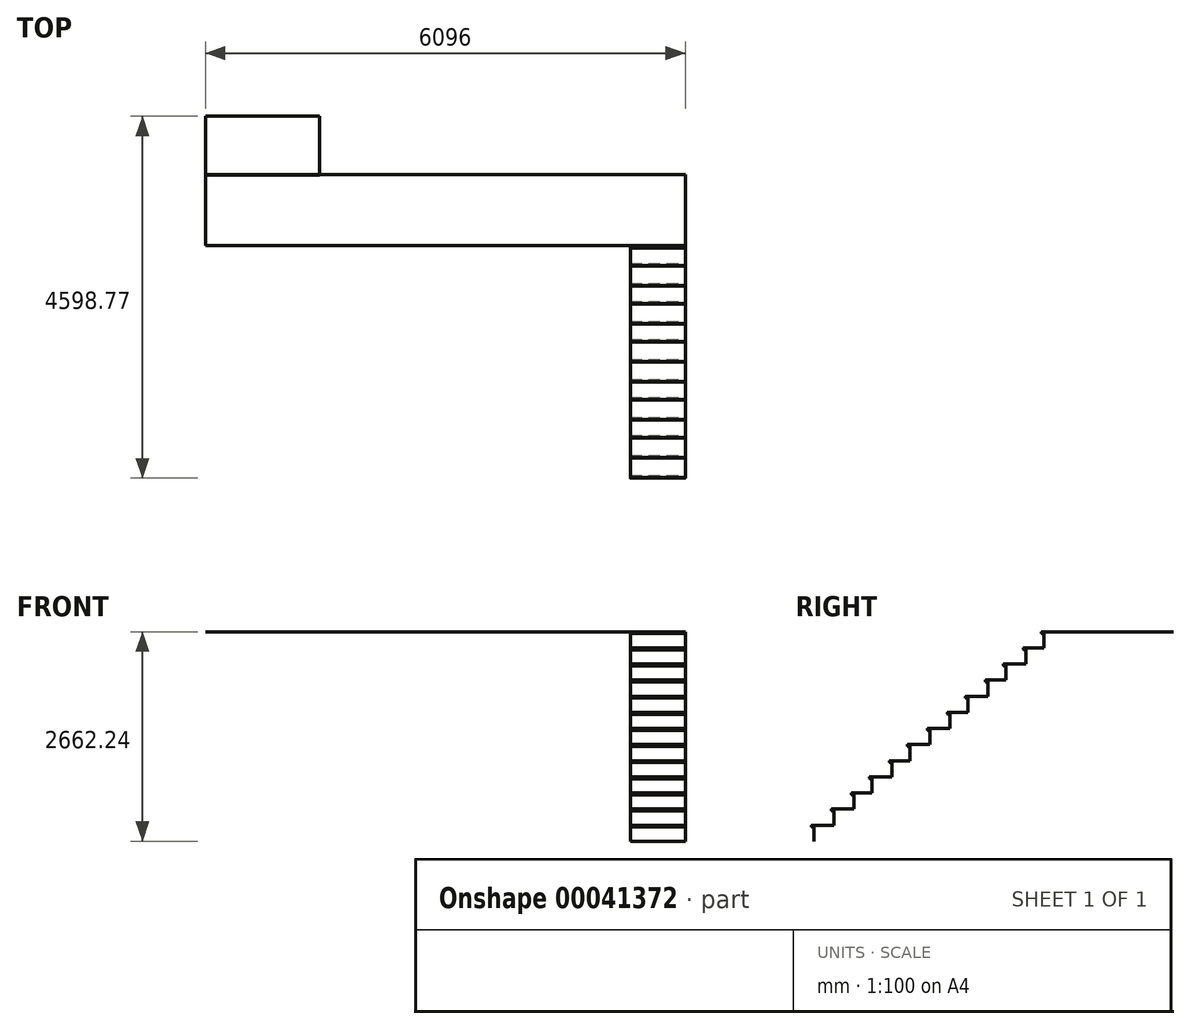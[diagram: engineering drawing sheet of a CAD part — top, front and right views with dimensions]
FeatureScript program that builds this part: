
annotation { "Feature Type Name" : "Feature", "Feature Type Description" : "" }
export const myFeature = defineFeature(function(context is Context, id is Id, definition is map)
    precondition{}
    {
        {
            var Q0;
            Q0=qCreatedBy(makeId("Top.planeOp"),FACE);
            var sketch = newSketch(context, id + "F0", { "sketchPlane" : qUnion([Q0])});
            skLineSegment(sketch, "E0", {"start": v(0, 0) * mm, "end": v(0, 1644.65) * mm});
            skLineSegment(sketch, "E1", {"start": v(0, 1644.65) * mm, "end": v(1447.8, 1644.65) * mm});
            skLineSegment(sketch, "E2", {"start": v(1447.8, 1644.65) * mm, "end": v(1447.8, 895.35) * mm});
            skLineSegment(sketch, "E3", {"start": v(1447.8, 895.35) * mm, "end": v(6096, 895.35) * mm});
            skLineSegment(sketch, "E4", {"start": v(6096, 895.35) * mm, "end": v(6096, 0) * mm});
            skLineSegment(sketch, "E5", {"start": v(0, 0) * mm, "end": v(5397.5, 0) * mm});
            skSolve(sketch);
        }
        {
            var Q0;
            Q0=qCreatedBy(makeId("Right.planeOp"),FACE);
            var Q1;
            Q1=sQuery(id+"F0.wireOp",VERTEX,"E5.end");
            cPlane(context, id + "F1", {"entities" : qUnion([Q0, Q1]), "cplaneType" : CPlaneType.PLANE_POINT, "offset" : 152.4 * mm, "width" : 152.4 * mm, "height" : 152.4 * mm});
        }
        {
            var Q0;
            Q0=qCreatedBy(id+"F1.planeOp",FACE);
            var sketch = newSketch(context, id + "F2", { "sketchPlane" : qUnion([Q0])});
            skLineSegment(sketch, "E6", {"start": v(-25.4, 0) * mm, "end": v(0, 0) * mm});
            skLineSegment(sketch, "E7", {"start": v(-25.4, -23.81) * mm, "end": v(0, -23.81) * mm});
            skLineSegment(sketch, "E8", {"start": v(0, -23.81) * mm, "end": v(0, -204.79) * mm});
            skArc(sketch, "E9", {"start": v(-25.4, 0) * mm, "mid": v(-31.75, -11.9) * mm, "end": v(-25.4, -23.81) * mm});
            skLineSegment(sketch, "E10", {"start": v(-31.75, -11.9) * mm, "end": v(-31.75, 17.78) * mm, "construction": true});
            skLineSegment(sketch, "E11", {"start": v(0, -204.79) * mm, "end": v(-254, -204.79) * mm});
            skArc(sketch, "E12", {"start": v(-254, -204.79) * mm, "mid": v(-260.35, -216.7) * mm, "end": v(-254, -228.6) * mm});
            skLineSegment(sketch, "E13", {"start": v(-254, -228.6) * mm, "end": v(-228.6, -228.6) * mm});
            skLineSegment(sketch, "E14", {"start": v(-228.6, -228.6) * mm, "end": v(-228.6, -409.58) * mm});
            skLineSegment(sketch, "E15", {"start": v(-228.6, -409.58) * mm, "end": v(-482.6, -409.58) * mm});
            skLineSegment(sketch, "E16", {"start": v(-260.35, -216.7) * mm, "end": v(-260.35, -170.19) * mm, "construction": true});
            skLineSegment(sketch, "E17", {"start": v(-482.6, -433.39) * mm, "end": v(-482.6, -614.36) * mm});
            skLineSegment(sketch, "E18", {"start": v(-711.2, -819.15) * mm, "end": v(-965.2, -819.15) * mm});
            skLineSegment(sketch, "E19", {"start": v(-482.6, -614.36) * mm, "end": v(-736.6, -614.36) * mm});
            skLineSegment(sketch, "E20", {"start": v(-711.2, -638.18) * mm, "end": v(-711.2, -819.15) * mm});
            skLineSegment(sketch, "E21", {"start": v(-742.95, -940.84) * mm, "end": v(-742.95, -626.27) * mm, "construction": true});
            skArc(sketch, "E22", {"start": v(-736.6, -614.36) * mm, "mid": v(-742.95, -626.27) * mm, "end": v(-736.6, -638.18) * mm});
            skLineSegment(sketch, "E23", {"start": v(-736.6, -638.18) * mm, "end": v(-711.2, -638.18) * mm});
            skArc(sketch, "E24", {"start": v(-508, -409.58) * mm, "mid": v(-514.35, -421.48) * mm, "end": v(-508, -433.39) * mm});
            skLineSegment(sketch, "E25", {"start": v(-508, -433.39) * mm, "end": v(-482.6, -433.39) * mm});
            skLineSegment(sketch, "E26", {"start": v(-508, -409.58) * mm, "end": v(-482.6, -409.58) * mm});
            skLineSegment(sketch, "E27", {"start": v(-514.35, -752.87) * mm, "end": v(-514.35, -421.48) * mm, "construction": true});
            skLineSegment(sketch, "E28", {"start": v(-1473.2, -1252.54) * mm, "end": v(-1447.8, -1252.54) * mm});
            skLineSegment(sketch, "E29", {"start": v(-1479.55, -1790.24) * mm, "end": v(-1479.55, -1240.63) * mm, "construction": true});
            skLineSegment(sketch, "E30", {"start": v(-965.2, -842.96) * mm, "end": v(-965.2, -1023.94) * mm});
            skLineSegment(sketch, "E31", {"start": v(-965.2, -1023.94) * mm, "end": v(-1219.2, -1023.94) * mm});
            skLineSegment(sketch, "E32", {"start": v(-1447.8, -1433.51) * mm, "end": v(-1701.8, -1433.51) * mm});
            skLineSegment(sketch, "E33", {"start": v(-1447.8, -1252.54) * mm, "end": v(-1447.8, -1433.51) * mm});
            skLineSegment(sketch, "E34", {"start": v(-1193.8, -1228.73) * mm, "end": v(-1447.8, -1228.73) * mm});
            skLineSegment(sketch, "E35", {"start": v(-1193.8, -1047.75) * mm, "end": v(-1193.8, -1228.73) * mm});
            skArc(sketch, "E36", {"start": v(-1473.2, -1228.73) * mm, "mid": v(-1479.55, -1240.63) * mm, "end": v(-1473.2, -1252.54) * mm});
            skLineSegment(sketch, "E37", {"start": v(-1473.2, -1228.73) * mm, "end": v(-1447.8, -1228.73) * mm});
            skArc(sketch, "E38", {"start": v(-1219.2, -1023.94) * mm, "mid": v(-1225.55, -1035.84) * mm, "end": v(-1219.2, -1047.75) * mm});
            skLineSegment(sketch, "E39", {"start": v(-1225.55, -1207.55) * mm, "end": v(-1225.55, -1035.84) * mm, "construction": true});
            skLineSegment(sketch, "E40", {"start": v(-1219.2, -1047.75) * mm, "end": v(-1193.8, -1047.75) * mm});
            skLineSegment(sketch, "E41", {"start": v(-990.6, -842.96) * mm, "end": v(-965.2, -842.96) * mm});
            skArc(sketch, "E42", {"start": v(-990.6, -819.15) * mm, "mid": v(-996.95, -831.06) * mm, "end": v(-990.6, -842.96) * mm});
            skLineSegment(sketch, "E43", {"start": v(-996.95, -1019.59) * mm, "end": v(-996.95, -831.06) * mm, "construction": true});
            skLineSegment(sketch, "E44", {"start": v(-990.6, -819.15) * mm, "end": v(-965.2, -819.15) * mm});
            skLineSegment(sketch, "E45", {"start": v(-2413, -2252.66) * mm, "end": v(-2667, -2252.66) * mm});
            skLineSegment(sketch, "E46", {"start": v(-2667, -2457.45) * mm, "end": v(-2921, -2457.45) * mm});
            skLineSegment(sketch, "E47", {"start": v(-2216.15, -1855) * mm, "end": v(-2216.15, -1794.57) * mm, "construction": true});
            skLineSegment(sketch, "E48", {"start": v(-2184.4, -1866.9) * mm, "end": v(-2184.4, -2047.88) * mm});
            skLineSegment(sketch, "E49", {"start": v(-2698.75, -2565.22) * mm, "end": v(-2698.75, -2264.57) * mm, "construction": true});
            skLineSegment(sketch, "E50", {"start": v(-1701.8, -1638.3) * mm, "end": v(-1955.8, -1638.3) * mm});
            skLineSegment(sketch, "E51", {"start": v(-1930.4, -1662.11) * mm, "end": v(-1930.4, -1843.09) * mm});
            skLineSegment(sketch, "E52", {"start": v(-1962.15, -1715.82) * mm, "end": v(-1962.15, -1650.2) * mm, "construction": true});
            skLineSegment(sketch, "E53", {"start": v(-1733.55, -1527.85) * mm, "end": v(-1733.55, -1445.42) * mm, "construction": true});
            skLineSegment(sketch, "E54", {"start": v(-1930.4, -1843.09) * mm, "end": v(-2184.4, -1843.09) * mm});
            skLineSegment(sketch, "E55", {"start": v(-2184.4, -2047.88) * mm, "end": v(-2438.4, -2047.88) * mm});
            skLineSegment(sketch, "E56", {"start": v(-1701.8, -1457.33) * mm, "end": v(-1701.8, -1638.3) * mm});
            skLineSegment(sketch, "E57", {"start": v(-2667, -2276.48) * mm, "end": v(-2667, -2457.45) * mm});
            skLineSegment(sketch, "E58", {"start": v(-2413, -2071.69) * mm, "end": v(-2413, -2252.66) * mm});
            skLineSegment(sketch, "E59", {"start": v(-2444.75, -2059.78) * mm, "end": v(-2444.75, -1982.54) * mm, "construction": true});
            skArc(sketch, "E60", {"start": v(-2692.4, -2252.66) * mm, "mid": v(-2698.75, -2264.57) * mm, "end": v(-2692.4, -2276.48) * mm});
            skLineSegment(sketch, "E61", {"start": v(-2692.4, -2276.48) * mm, "end": v(-2667, -2276.48) * mm});
            skLineSegment(sketch, "E62", {"start": v(-2692.4, -2252.66) * mm, "end": v(-2667, -2252.66) * mm});
            skLineSegment(sketch, "E63", {"start": v(-2209.8, -1866.9) * mm, "end": v(-2184.4, -1866.9) * mm});
            skArc(sketch, "E64", {"start": v(-1955.8, -1638.3) * mm, "mid": v(-1962.15, -1650.2) * mm, "end": v(-1955.8, -1662.11) * mm});
            skLineSegment(sketch, "E65", {"start": v(-1955.8, -1662.11) * mm, "end": v(-1930.4, -1662.11) * mm});
            skLineSegment(sketch, "E66", {"start": v(-2438.4, -2071.69) * mm, "end": v(-2413, -2071.69) * mm});
            skLineSegment(sketch, "E67", {"start": v(-2209.8, -1843.09) * mm, "end": v(-2184.4, -1843.09) * mm});
            skArc(sketch, "E68", {"start": v(-2438.4, -2047.88) * mm, "mid": v(-2444.75, -2059.78) * mm, "end": v(-2438.4, -2071.69) * mm});
            skArc(sketch, "E69", {"start": v(-2209.8, -1843.09) * mm, "mid": v(-2216.15, -1855) * mm, "end": v(-2209.8, -1866.9) * mm});
            skLineSegment(sketch, "E70", {"start": v(-1727.2, -1457.33) * mm, "end": v(-1701.8, -1457.33) * mm});
            skArc(sketch, "E71", {"start": v(-1727.2, -1433.51) * mm, "mid": v(-1733.55, -1445.42) * mm, "end": v(-1727.2, -1457.33) * mm});
            skLineSegment(sketch, "E72", {"start": v(-1727.2, -1433.51) * mm, "end": v(-1701.8, -1433.51) * mm});
            skLineSegment(sketch, "E73", {"start": v(-2946.4, -2481.26) * mm, "end": v(-2921, -2481.26) * mm});
            skLineSegment(sketch, "E74", {"start": v(-2952.75, -2664.36) * mm, "end": v(-2952.75, -2469.36) * mm, "construction": true});
            skLineSegment(sketch, "E75", {"start": v(-2921, -2481.26) * mm, "end": v(-2921, -2662.24) * mm});
            skArc(sketch, "E76", {"start": v(-2946.4, -2457.45) * mm, "mid": v(-2952.75, -2469.36) * mm, "end": v(-2946.4, -2481.26) * mm});
            skLineSegment(sketch, "E77", {"start": v(-2946.4, -2457.45) * mm, "end": v(-2921, -2457.45) * mm});
            skSolve(sketch);
        }
        {
            var Q0;
            Q0 = qConstructionFilter(qBodyType(qCreatedBy(id + "F2" ,EDGE), BodyType.WIRE), ConstructionObject.NO);
            extrude(context, id + "F3", {"bodyType" : ToolBodyType.SURFACE, "surfaceEntities" : qUnion([Q0]), "depth" : 698.5 * mm});
        }
        {
            var Q0;
            Q0=qCreatedBy(id+"F1.planeOp",FACE);
            var Q1;
            Q1=sQuery(id+"F0.wireOp",VERTEX,"E3.end");
            cPlane(context, id + "F4", {"entities" : qUnion([Q0, Q1]), "cplaneType" : CPlaneType.PLANE_POINT, "offset" : 152.4 * mm, "width" : 152.4 * mm, "height" : 152.4 * mm});
        }
        {
            var Q0;
            Q0=qCreatedBy(id+"F4.planeOp",FACE);
            var sketch = newSketch(context, id + "F5", { "sketchPlane" : qUnion([Q0])});
            skLineSegment(sketch, "E78", {"start": v(0, 0) * mm, "end": v(903.36, 0) * mm});
            skSolve(sketch);
        }
        {
            var Q0;
            Q0=sQuery(id+"F5.wireOp",EDGE,"E78");
            extrude(context, id + "F6", {"bodyType" : ToolBodyType.SURFACE, "surfaceEntities" : qUnion([Q0]), "oppositeDirection" : true, "depth" : 6096 * mm});
        }
        {
            var Q0;
            Q0=qCreatedBy(makeId("Right.planeOp"),FACE);
            var Q1;
            Q1=sQuery(id+"F0.wireOp",VERTEX,"E2.start");
            cPlane(context, id + "F7", {"entities" : qUnion([Q0, Q1]), "cplaneType" : CPlaneType.PLANE_POINT, "offset" : 152.4 * mm, "width" : 152.4 * mm, "height" : 152.4 * mm});
        }
        {
            var Q0;
            Q0=qCreatedBy(id+"F7.planeOp",FACE);
            var sketch = newSketch(context, id + "F8", { "sketchPlane" : qUnion([Q0])});
            skPoint(sketch, "E79.0", {"position": v(895.35, 0) * mm});
            skLineSegment(sketch, "E80", {"start": v(895.35, 0) * mm, "end": v(1646.02, 0) * mm});
            skSolve(sketch);
        }
        {
            var Q0;
            Q0 = qSketchRegion(id + "F8", true);
            var Q1;
            Q1=sQuery(id+"F8.wireOp",EDGE,"E80");
            extrude(context, id + "F9", {"entities" : qUnion([Q0]), "bodyType" : ToolBodyType.SURFACE, "surfaceEntities" : qUnion([Q1]), "oppositeDirection" : true, "depth" : 1447.8 * mm});
        }
    });
